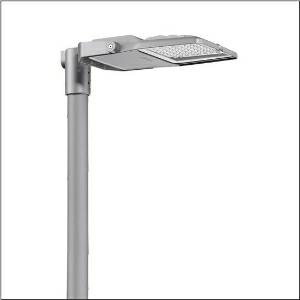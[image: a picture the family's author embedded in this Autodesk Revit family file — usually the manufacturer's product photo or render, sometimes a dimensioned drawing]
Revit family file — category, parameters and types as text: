
# Revit family: floodlight_fl_21_iq_mini___pl61_5xa7771d4c3a_f55b
name_source: partatom
category: Lighting Fixtures
units: mm (PartAtom-declared; Revit-internal decimal feet)

## family parameters
Cut with Voids When Loaded = No
Host = Face
Light Source = No
Part Type = Normal
Room Calculation Point = No
Round Connector Dimension = Use Diameter
Shared = No

## types (1)
- --- (1 x LED, 18260 lm, 143 W, 4000K)
    Apparent Load = 143 VA
    CIE Flux Codes = 33 65 98 100 100
    Color Rendering = 70
    Color Temperature = 4000K
    Default Elevation = 1800 mm
    Description = Floodlight FL 21 iQ mini, floodlight, primary light control with lens, of PMMA, primary optical cover: protective disc, of toughened safety glass, transparent, light distribution: PL61, light emission: direct distribution, installation type: surface-mounted, LED, High Power LED, rated luminous flux: 18.260lm, luminous efficacy: 128lm/W, light colour: 740, colour temperature: 4000K, control gear: iQ Comfort/DALI, control: Auto-Match, Temp-Guard, Lumen-Switch, Night-Set, Smart-Wire, Light-Fading, Desk-Remote (wireless, voltage-free reading and setting of iQ features in the workshop via application-optimized NFC function/RFID function), optimised constant luminous flux control (CLO 2.0), with terminal, 6-pole, mains connection: 220..240V, AC, 50/60Hz, start of lifetime: 143W, end of service life: 152W, reduction: 61W, luminaire housing, of diecast aluminium, powder-coated, Siteco® metallic grey (DB 702S), corrosivity category C5 mid according to DIN EN ISO 12944, suitable for swimming pools, chlorine-resistant, sealing non-destructively replaceable, please order mast flange separately, mast bracket, of steel, galvanised, powder-coated, Siteco® metallic grey (DB 702S), protection rating (complete): IP66, insulation class (complete): insulation class II (safety insulation), certification: CE, ENEC, VDE, protection symbol: D, impact resistance: IK08, permissible operating ambient temperature: -40..+40°C, permissible operating ambient temperature for outdoor applications: -40..+50°C, standard: DIN EN 12944, LABS conformity tested according to VDMA 24364:2018-05, packaging unit: 1 piece

Light Distribution: PL61
    Height = 70 mm
    Lamp = 1 x LED
    Lamp Light Flux = 18260 lm
    Lamp Power = 143 W
    Lamp count = 1
    Length = 485 mm
    Luminous efficacy = 128 lm/W
    Manufacturer = Siteco
    ModVariant = No
    Model = 5XA7771D4C3A
    Number of Poles = 1
    OnlyDefault = Yes
    Power Factor = 1
    Product Name = Floodlight FL 21 iQ mini | PL61
    Product group = floodlight | pylon annexe
    ProductGroupID = 6201
    Protection Class = Protection class II
    Protection Degree = IP 66
    RLX_Detail_Level = 1
    RLX_Emergency_Light_Flux = 0 lm
    RLX_Emergency_Type = 0
    RLX_Emergency_Type_DB = No
    RlxData = <blob elided: 101781 chars, md5=ccf06cfc>
    Socket = socket
    Standby Power = 0 W
    System Light Flux = 18260 lm
    System Power = 143 W
    Type Comments = factory setting: luminous flux: 100 % | dim-lin: 254 | 730 mA
    Type Image = l_1007125.jpg
    URL = http://relux.com
    VarID = @adj_194077
    Voltage = 0 V
    Weight = 0.00 kg
    Width = 337 mm

## geometry (parser evidence)
native form markers: Blend x4, Sweep x13
no freeform markers — native parametric forms only
